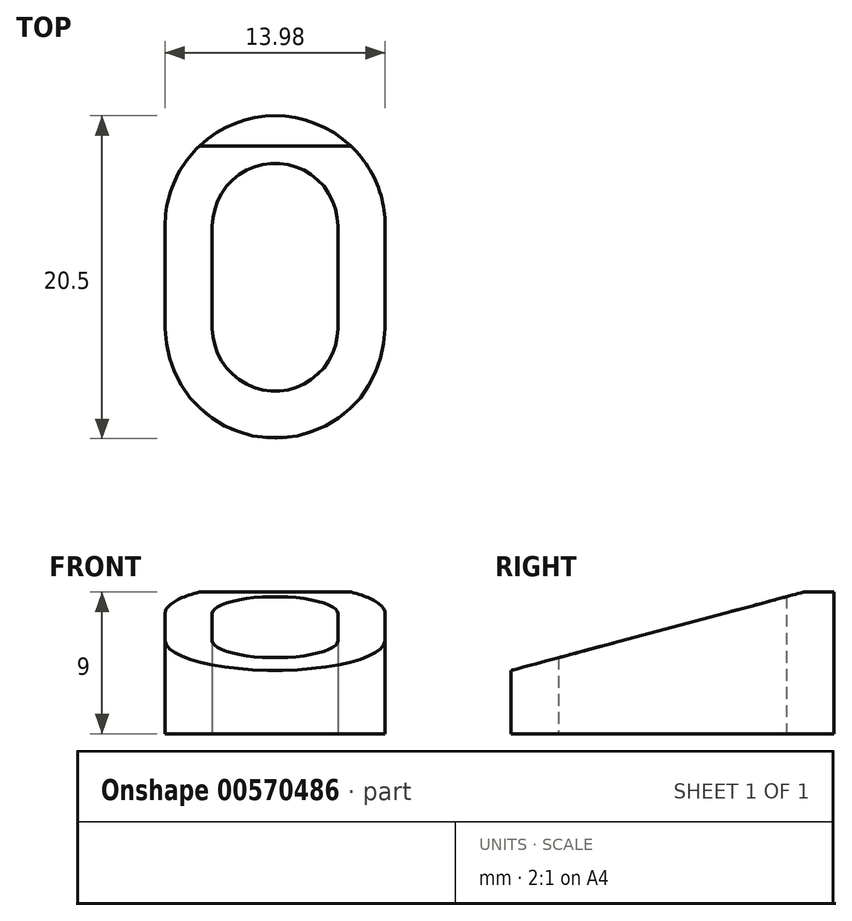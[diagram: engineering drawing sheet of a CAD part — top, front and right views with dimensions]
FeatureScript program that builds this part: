
annotation { "Feature Type Name" : "Feature", "Feature Type Description" : "" }
export const myFeature = defineFeature(function(context is Context, id is Id, definition is map)
    precondition{}
    {
        {
            var Q0;
            Q0=qCreatedBy(makeId("Top.planeOp"),FACE);
            var sketch = newSketch(context, id + "F0", { "sketchPlane" : qUnion([Q0])});
            skLineSegment(sketch, "E0", {"start": v(0, 24.6) * mm, "end": v(0, -24.55) * mm, "construction": true});
            skLineSegment(sketch, "E1", {"start": v(22, 0) * mm, "end": v(-21.86, 0) * mm, "construction": true});
            skArc(sketch, "E2", {"start": v(3.99, 3.26) * mm, "mid": v(0, 7.25) * mm, "end": v(-4, 3.26) * mm});
            skLineSegment(sketch, "E3", {"start": v(-4, 3.26) * mm, "end": v(-4, 0) * mm});
            skLineSegment(sketch, "E4", {"start": v(4, 3.26) * mm, "end": v(4, 0) * mm});
            skLineSegment(sketch, "E5.MirrorCS", {"start": v(-4, -3.26) * mm, "end": v(-4, 0) * mm});
            skArc(sketch, "E6.MirrorCS", {"start": v(3.99, -3.26) * mm, "mid": v(0, -7.25) * mm, "end": v(-4, -3.26) * mm});
            skLineSegment(sketch, "E7.MirrorCS", {"start": v(4, -3.26) * mm, "end": v(4, 0) * mm});
            skLineSegment(sketch, "E8.0", {"start": v(7, -3.26) * mm, "end": v(7, 0) * mm});
            skLineSegment(sketch, "E8.1", {"start": v(-7, -3.26) * mm, "end": v(-7, 0) * mm});
            skLineSegment(sketch, "E8.2", {"start": v(-7, 3.26) * mm, "end": v(-7, 0) * mm});
            skArc(sketch, "E8.3", {"start": v(7, -3.26) * mm, "mid": v(0, -10.25) * mm, "end": v(-7, -3.26) * mm});
            skArc(sketch, "E8.4", {"start": v(7, 3.26) * mm, "mid": v(0, 10.25) * mm, "end": v(-7, 3.26) * mm});
            skLineSegment(sketch, "E8.5", {"start": v(7, 3.26) * mm, "end": v(7, 0) * mm});
            skSolve(sketch);
        }
        {
            var Q0;
            Q0=makeQuery(id+"F0.imprint","IMPRINT",FACE,{"disambiguationData":[TD([[makeQuery(id+"F0.imprint","IMPRINT",EDGE,{"derivedFrom":sQuery(id+"F0.wireOp",EDGE,"E2")}),-1.0]])]});
            var Q1;
            Q1 = qConstructionFilter(qBodyType(qCreatedBy(id + "F0" ,EDGE), BodyType.WIRE), ConstructionObject.NO);
            extrude(context, id + "F1", {"entities" : qUnion([Q0]), "surfaceEntities" : qUnion([Q1]), "depth" : 9 * mm, "offsetDistance" : 25 * mm});
        }
        {
            var Q0;
            Q0=makeQuery(id+"F1.opExtrude","CAP_FACE",FACE,{"disambiguationData":[OSD([sQuery(id+"F0.wireOp",EDGE,"E2"),sQuery(id+"F0.wireOp",EDGE,"E3"),sQuery(id+"F0.wireOp",EDGE,"E4"),sQuery(id+"F0.wireOp",EDGE,"E5.MirrorCS"),sQuery(id+"F0.wireOp",EDGE,"E6.MirrorCS"),sQuery(id+"F0.wireOp",EDGE,"E7.MirrorCS"),sQuery(id+"F0.wireOp",EDGE,"E8.0"),sQuery(id+"F0.wireOp",EDGE,"E8.1"),sQuery(id+"F0.wireOp",EDGE,"E8.2"),sQuery(id+"F0.wireOp",EDGE,"E8.3"),sQuery(id+"F0.wireOp",EDGE,"E8.4"),sQuery(id+"F0.wireOp",EDGE,"E8.5")])],"isStart":false});
            var sketch = newSketch(context, id + "F2", { "sketchPlane" : qUnion([Q0])});
            skLineSegment(sketch, "E9", {"start": v(7, -3.26) * mm, "end": v(-7, -3.26) * mm, "construction": true});
            skSolve(sketch);
        }
        {
            var Q0;
            Q0=sQuery(id+"F2.wireOp",EDGE,"E9");
            cPlane(context, id + "F3", {"entities" : qUnion([Q0]), "cplaneType" : CPlaneType.LINE_ANGLE, "offset" : 25 * mm, "angle" : 75 * degree, "width" : 150 * mm, "height" : 150 * mm});
        }
        {
            var Q0;
            Q0=qCreatedBy(id+"F3.planeOp",FACE);
            cPlane(context, id + "F4", {"entities" : qUnion([Q0]), "cplaneType" : CPlaneType.OFFSET, "offset" : 10 * mm, "width" : 150 * mm, "height" : 150 * mm});
        }
        {
            var Q0;
            Q0=qCreatedBy(id+"F4.planeOp",FACE);
            var sketch = newSketch(context, id + "F5", { "sketchPlane" : qUnion([Q0])});
            skLineSegment(sketch, "E10.bottom", {"start": v(-23, -11.47) * mm, "end": v(19.87, -11.47) * mm});
            skLineSegment(sketch, "E10.top", {"start": v(-23, 21.28) * mm, "end": v(19.87, 21.28) * mm});
            skLineSegment(sketch, "E10.left", {"start": v(-23, -11.47) * mm, "end": v(-23, 21.28) * mm});
            skLineSegment(sketch, "E10.right", {"start": v(19.87, -11.47) * mm, "end": v(19.87, 21.28) * mm});
            skSolve(sketch);
        }
        {
            var Q0;
            Q0 = qSketchRegion(id + "F5", true);
            extrude(context, id + "F6", {"entities" : qUnion([Q0]), "operationType" : NewBodyOperationType.REMOVE, "oppositeDirection" : true, "depth" : 13 * mm, "offsetDistance" : 25 * mm});
        }
    });
